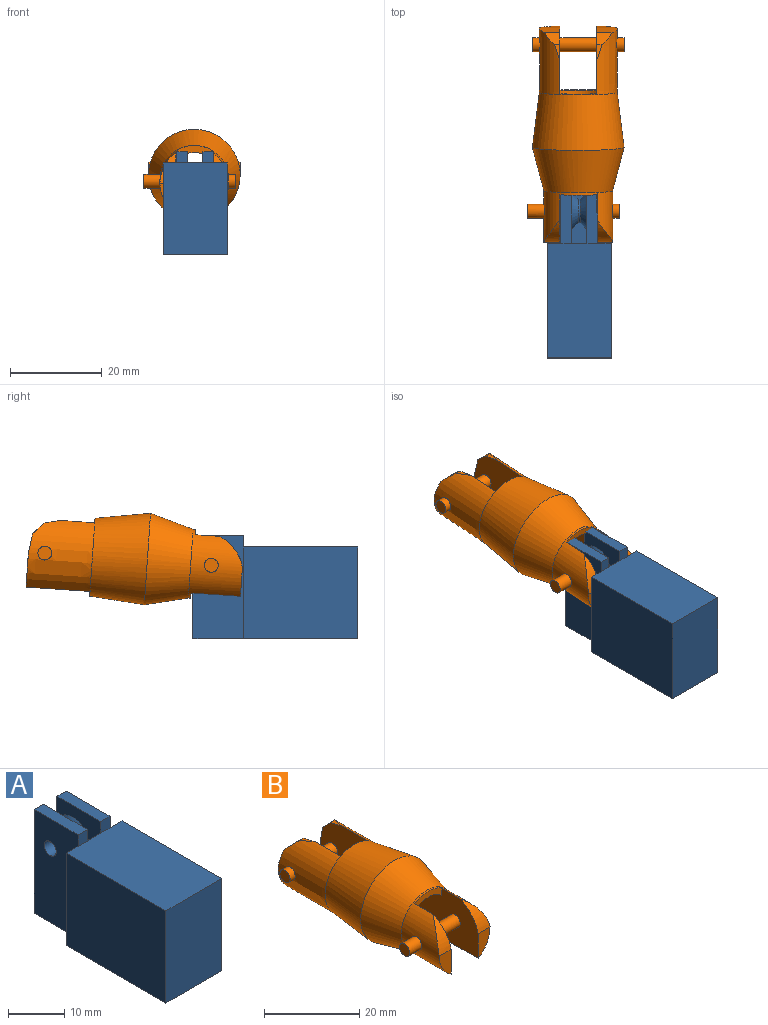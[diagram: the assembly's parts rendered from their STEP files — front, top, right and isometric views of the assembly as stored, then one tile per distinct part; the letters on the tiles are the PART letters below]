
ASSEMBLY  parts=2 mates=1
PART A: 22 faces, bbox 14x36x22.5 mm
  f0: plane 2.5x2.3mm, normal (0,-1,0), area 5.7mm2, adj f3,f4,f5,f13
  f1: plane 2.5x2.3mm, normal (0,-1,0), area 5.7mm2, adj f8,f9,f10,f13
  f2: plane 11x3.4mm, normal (0,0,1), area 37.4mm2, adj f3,f7,f8,f12
  f3: plane 12.7x11mm, normal (1,0,0), area 89.4mm2, adj f0,f2,f4,f7,f12,f20
  f4: plane 11x2.3mm, normal (0,0,1), area 25.3mm2, adj f0,f3,f5,f7
  f5: plane 22.5x11mm, normal (-1,0,0), area 240.4mm2, adj f0,f4,f6,f7,f17,f18
  f6: plane 36x14mm, normal (0,0,-1), area 438mm2, adj f5,f7,f10,f11,f14,f15,f16,f17
  f7: plane 22.5x8mm, normal (0,1,0), area 136.8mm2, adj f2,f3,f4,f5,f6,f8,f9,f10
  f8: plane 12.7x11mm, normal (-1,0,0), area 89.4mm2, adj f1,f2,f7,f9,f12,f21
  f9: plane 11x2.3mm, normal (0,0,1), area 25.3mm2, adj f1,f7,f8,f10
  f10: plane 22.5x11mm, normal (1,0,0), area 240.4mm2, adj f1,f6,f7,f9,f11,f18
  f11: plane 20x3mm, normal (0,1,0), area 60mm2, adj f6,f10,f13,f15
  f12: plane 10.2x3.4mm, normal (0,1,0), area 34.7mm2, adj f2,f3,f8,f13
  f13: plane 25x14mm, normal (0,0,1), area 350mm2, adj f0,f1,f11,f12,f14,f15,f16,f17
  f14: plane 25x20mm, normal (-1,0,0), area 500mm2, adj f6,f13,f16,f17
  f15: plane 25x20mm, normal (1,0,0), area 500mm2, adj f6,f11,f13,f16
  f16: plane 20x14mm, normal (0,-1,0), area 280mm2, adj f6,f13,f14,f15
  f17: plane 20x3mm, normal (0,1,0), area 60mm2, adj f5,f6,f13,f14
  f18: cylinder r=1.5mm len=8mm, axis (1,0,0), area 75.4mm2, adj f5,f10
  f19: cylinder r=2.5mm len=5mm, axis (1,0,0), area 6.3mm2, adj f20,f21
  f20: cone r=2.5mm half-angle=45deg, axis (-1,0,0), area 43.3mm2, adj f3,f19
  f21: cone r=2.5mm half-angle=45deg, axis (1,0,0), area 43.3mm2, adj f8,f19
PART B: 35 faces, bbox 21.2x47x20.2 mm
  f0: cylinder r=1.5mm len=3mm, axis (-1,0,0), area 14.9mm2, adj f1,f5
  f1: plane 3x3mm, normal (1,0,0), area 7.1mm2, adj f0
  f2: plane 7.54x4.51mm, normal (0,1,0), area 24mm2, adj f7,f18,f26
  f3: plane 7.54x4.51mm, normal (0,1,0), area 24mm2, adj f8,f17,f21
  f4: plane 6.34x3.5mm, normal (0,-1,0), area 15.7mm2, adj f5,f7,f20
  f5: cylinder r=7.5mm len=15mm, axis (0,-1,0), area 297.2mm2, adj f0,f4,f6,f7,f8,f13,f14,f15
  f6: plane 6.34x3.5mm, normal (0,-1,0), area 15.7mm2, adj f5,f8,f19
  f7: plane 46.8x15mm, normal (1,0,0), area 508.3mm2, adj f2,f4,f5,f9,f10,f11,f12,f13
  f8: plane 46.8x15mm, normal (-1,0,0), area 508.3mm2, adj f3,f5,f6,f9,f10,f11,f12,f13
  f9: plane 8.03x4mm, normal (0,1,0), area 20.9mm2, adj f7,f8,f11,f16
  f10: plane 8.03x4.09mm, normal (0,1,0), area 21.6mm2, adj f7,f8,f12,f16
  f11: cylinder r=6mm len=22mm, axis (0,-1,0), area 192.6mm2, adj f7,f8,f9,f13
  f12: cylinder r=6mm len=22mm, axis (0,-1,0), area 192.6mm2, adj f7,f8,f10,f14
  f13: plane 8x3.03mm, normal (0,-1,0), area 12.9mm2, adj f5,f7,f8,f11
  f14: plane 8x3.03mm, normal (0,-1,0), area 12.9mm2, adj f5,f7,f8,f12
  f15: bspline ~19.99x19.99mm, area 540.1mm2, adj f5,f16
  f16: bspline ~19.99x19.98mm, area 702.9mm2, adj f9,f10,f15,f17,f18
  f17: extruded ~15x14mm, area 236.2mm2, adj f3,f8,f16,f21,f22,f23,f28
  f18: extruded ~15x14mm, area 236.2mm2, adj f2,f7,f16,f24,f25,f26,f30
  f19: cylinder r=9.25mm len=6.34mm, axis (1,0,0), area 15.1mm2, adj f5,f6,f8
  f20: cylinder r=9.25mm len=6.34mm, axis (1,0,0), area 15.1mm2, adj f4,f5,f7
  f21: plane 4.53x4.29mm, normal (0,0.99,0.16), area 17.8mm2, adj f3,f8,f17,f22
  f22: plane 3.52x2.62mm, normal (0,0.72,0.69), area 8.2mm2, adj f8,f17,f21,f23
  f23: plane 3.56x1.31mm, normal (0,0.22,0.98), area 2.3mm2, adj f8,f17,f22
  f24: plane 3.56x1.31mm, normal (0,0.22,0.98), area 2.3mm2, adj f7,f18,f25
  f25: plane 3.52x2.62mm, normal (0,0.72,0.69), area 8.2mm2, adj f7,f18,f24,f26
  f26: plane 4.53x4.29mm, normal (0,0.99,0.16), area 17.8mm2, adj f2,f7,f18,f25
  f27: plane 3x3mm, normal (1,0,0), area 7.1mm2, adj f28
  f28: cylinder r=1.5mm len=3mm, axis (-1,0,0), area 14.6mm2, adj f17,f27
  f29: cylinder r=1.5mm len=8mm, axis (-1,0,0), area 75.4mm2, adj f7,f8
  f30: cylinder r=1.5mm len=3mm, axis (-1,0,0), area 14.6mm2, adj f18,f31
  f31: plane 3x3mm, normal (-1,0,0), area 7.1mm2, adj f30
  f32: cylinder r=1.5mm len=8mm, axis (-1,0,0), area 75.4mm2, adj f7,f8
  f33: plane 3x3mm, normal (-1,0,0), area 7.1mm2, adj f34
  f34: cylinder r=1.5mm len=3.66mm, axis (-1,0,0), area 33.4mm2, adj f5,f33
PLACE A t=(-12.09,8.32,-16.54)mm fixed
PLACE B rot(axis=(1,0,0),3.9deg) t=(-12.29,9.4,-16.23)mm
MATE revolute B.f0 <-> A.f18  axis (-1,0,0) through (-12.29,4.32,-0.54)mm
